AUTODESK INVENTOR PART (.ipt)
format: ipt  version: 2021 (Build 250183000, 183)  size: 291,328 bytes
history: native  units: mm
features: extrude x3, sketch x3, other x1
ambient origin geometry x8: Origin, YZ Plane, XZ Plane, XY Plane, X Axis, Y Axis, Z Axis, Center Point
bodies: Volumenkörper1 (feature_tree)
feature tree (7):
  other  "Faden_Halter_24_Durchmesser"
  extrude  "Extrusion1"  Depth=5.0mm
  extrude  "Extrusion2"  Depth=2.5mm
  extrude  "Extrusion3"  Depth=6.0mm
  sketch  "Skizze1"  dims[d0=24.0mm d1=5.0mm]
  sketch  "Skizze2"  dims[d2=2.5mm d3=0.0mm d4=1.5mm]
  sketch  "Skizze3"  dims[d5=1.5mm d6=1.3mm d7=1.3mm d8=10.4mm d9=10.4mm d10=6.75mm d11=0.0mm d12=2.8mm d13=6.0mm d14=0.0mm d18=40.0mm d20=360.0deg d22=6.75mm d23=0.0mm d24=0.5mm d25=0.872665mm d26=0.5mm d27=0.872665mm]
